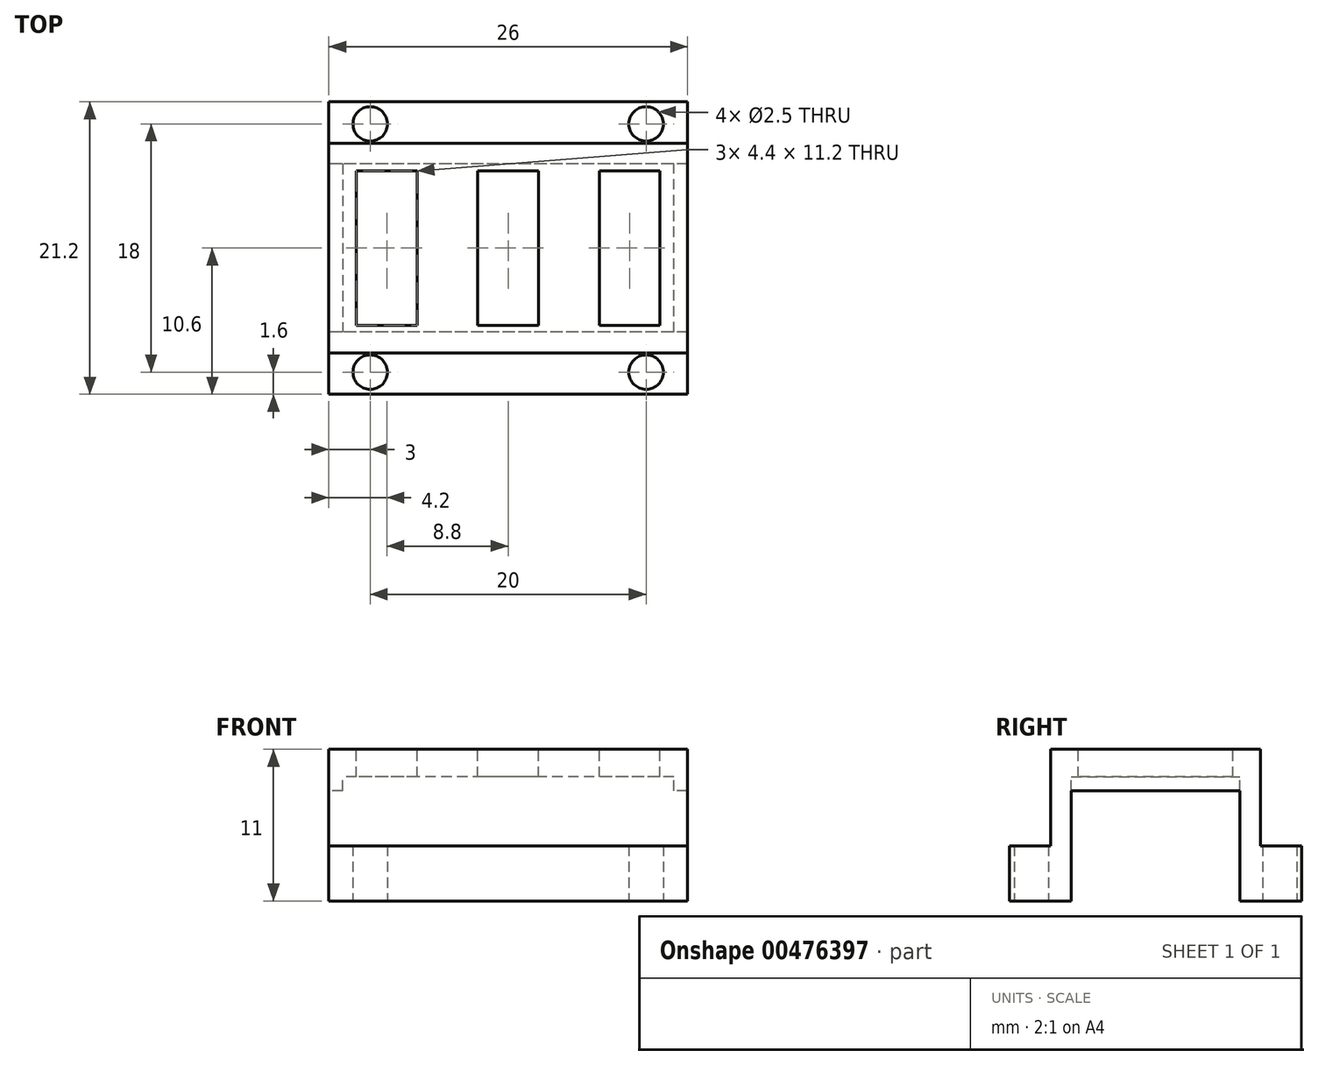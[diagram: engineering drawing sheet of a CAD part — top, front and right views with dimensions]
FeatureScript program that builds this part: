
annotation { "Feature Type Name" : "Feature", "Feature Type Description" : "" }
export const myFeature = defineFeature(function(context is Context, id is Id, definition is map)
    precondition{}
    {
        {
            var Q0;
            Q0=qCreatedBy(makeId("Right.planeOp"),FACE);
            var sketch = newSketch(context, id + "F0", { "sketchPlane" : qUnion([Q0])});
            skLineSegment(sketch, "E0", {"start": v(0, 0) * mm, "end": v(4.5, 0) * mm});
            skLineSegment(sketch, "E1", {"start": v(4.5, 0) * mm, "end": v(4.5, 9) * mm});
            skLineSegment(sketch, "E2", {"start": v(4.5, 9) * mm, "end": v(10.6, 9) * mm});
            skLineSegment(sketch, "E3", {"start": v(10.6, 9) * mm, "end": v(10.6, 11) * mm, "construction": true});
            skLineSegment(sketch, "E4", {"start": v(10.6, 11) * mm, "end": v(3, 11) * mm});
            skLineSegment(sketch, "E5", {"start": v(3, 11) * mm, "end": v(3, 4) * mm});
            skLineSegment(sketch, "E6", {"start": v(3, 4) * mm, "end": v(0, 4) * mm});
            skLineSegment(sketch, "E7", {"start": v(0, 4) * mm, "end": v(0, 0) * mm});
            skLineSegment(sketch, "E8.0.MirrorCS", {"start": v(21.2, 0) * mm, "end": v(16.7, 0) * mm});
            skLineSegment(sketch, "E8.1.MirrorCS", {"start": v(16.7, 0) * mm, "end": v(16.7, 9) * mm});
            skLineSegment(sketch, "E8.2.MirrorCS", {"start": v(16.7, 9) * mm, "end": v(10.6, 9) * mm});
            skLineSegment(sketch, "E8.3.MirrorCS", {"start": v(10.6, 11) * mm, "end": v(18.2, 11) * mm});
            skLineSegment(sketch, "E8.4.MirrorCS", {"start": v(18.2, 11) * mm, "end": v(18.2, 4) * mm});
            skLineSegment(sketch, "E8.5.MirrorCS", {"start": v(21.2, 4) * mm, "end": v(21.2, 0) * mm});
            skLineSegment(sketch, "E8.6.MirrorCS", {"start": v(18.2, 4) * mm, "end": v(21.2, 4) * mm});
            skSolve(sketch);
        }
        {
            var Q0;
            Q0=qSketchRegion(id+"F0",true);
            extrude(context, id + "F1", {"entities" : qUnion([Q0]), "depth" : 26 * mm});
        }
        {
            var Q0;
            Q0=makeQuery(id+"F1.opExtrude","SWEPT_FACE",FACE,{"disambiguationData":[OSD([sQuery(id+"F0.wireOp",EDGE,"E2"),sQuery(id+"F0.wireOp",EDGE,"E8.2.MirrorCS")])]});
            var sketch = newSketch(context, id + "F2", { "sketchPlane" : qUnion([Q0])});
            skLineSegment(sketch, "E9.bottom", {"start": v(0, -16.7) * mm, "end": v(1, -16.7) * mm});
            skLineSegment(sketch, "E9.top", {"start": v(0, -4.5) * mm, "end": v(1, -4.5) * mm});
            skLineSegment(sketch, "E9.left", {"start": v(0, -16.7) * mm, "end": v(0, -4.5) * mm});
            skLineSegment(sketch, "E9.right", {"start": v(1, -16.7) * mm, "end": v(1, -4.5) * mm});
            skLineSegment(sketch, "E10.bottom", {"start": v(26, -4.5) * mm, "end": v(25, -4.5) * mm});
            skLineSegment(sketch, "E10.top", {"start": v(26, -16.7) * mm, "end": v(25, -16.7) * mm});
            skLineSegment(sketch, "E10.left", {"start": v(26, -4.5) * mm, "end": v(26, -16.7) * mm});
            skLineSegment(sketch, "E10.right", {"start": v(25, -4.5) * mm, "end": v(25, -16.7) * mm});
            skSolve(sketch);
        }
        {
            var Q0;
            Q0=qSketchRegion(id+"F2",true);
            extrude(context, id + "F3", {"entities" : qUnion([Q0]), "operationType" : NewBodyOperationType.ADD, "depth" : 1 * mm});
        }
        {
            var Q0;
            Q0=makeQuery(id+"F1.opExtrude","SWEPT_FACE",FACE,{"disambiguationData":[OSD([sQuery(id+"F0.wireOp",EDGE,"E0")])]});
            var sketch = newSketch(context, id + "F4", { "sketchPlane" : qUnion([Q0])});
            skCircle(sketch, "E11", {"center": v(3, -1.6) * mm, "radius": 1.25 * mm});
            skLineSegment(sketch, "E12", {"start": v(13, 0) * mm, "end": v(13, -10.6) * mm, "construction": true});
            skLineSegment(sketch, "E13", {"start": v(13, -10.6) * mm, "end": v(0, -10.6) * mm, "construction": true});
            skLineSegment(sketch, "E14", {"start": v(0, -10.6) * mm, "end": v(0, 0) * mm, "construction": true});
            skLineSegment(sketch, "E15", {"start": v(0, -10.6) * mm, "end": v(0, -21.2) * mm, "construction": true});
            skCircle(sketch, "E16.0.MirrorC", {"center": v(23, -1.6) * mm, "radius": 1.25 * mm});
            skCircle(sketch, "E17.0.MirrorC", {"center": v(23, -19.6) * mm, "radius": 1.25 * mm});
            skCircle(sketch, "E17.1.MirrorC", {"center": v(3, -19.6) * mm, "radius": 1.25 * mm});
            skSolve(sketch);
        }
        {
            var Q0;
            Q0=qSketchRegion(id+"F4",true);
            extrude(context, id + "F5", {"entities" : qUnion([Q0]), "operationType" : NewBodyOperationType.REMOVE, "endBound" : BoundingType.UP_TO_NEXT, "oppositeDirection" : true, "depth" : 25 * mm});
        }
        {
            var Q0;
            Q0=makeQuery(id+"F1.opExtrude","SWEPT_FACE",FACE,{"disambiguationData":[OSD([sQuery(id+"F0.wireOp",EDGE,"E4"),sQuery(id+"F0.wireOp",EDGE,"E8.3.MirrorCS")])]});
            var sketch = newSketch(context, id + "F6", { "sketchPlane" : qUnion([Q0])});
            skLineSegment(sketch, "E18.bottom", {"start": v(6.4, 5) * mm, "end": v(10.8, 5) * mm, "construction": true});
            skLineSegment(sketch, "E18.left", {"start": v(2, 5) * mm, "end": v(2, 16.2) * mm});
            skLineSegment(sketch, "E18.right", {"start": v(10.8, 5) * mm, "end": v(10.8, 16.2) * mm});
            skLineSegment(sketch, "E19.top", {"start": v(10.8, 5) * mm, "end": v(15.2, 5) * mm});
            skLineSegment(sketch, "E19.left", {"start": v(10.8, 16.2) * mm, "end": v(10.8, 5) * mm});
            skLineSegment(sketch, "E20.bottom", {"start": v(15.2, 5) * mm, "end": v(19.6, 5) * mm, "construction": true});
            skLineSegment(sketch, "E20.left", {"start": v(15.2, 5) * mm, "end": v(15.2, 16.2) * mm});
            skLineSegment(sketch, "E20.right", {"start": v(19.6, 5) * mm, "end": v(19.6, 16.2) * mm});
            skLineSegment(sketch, "E21.bottom", {"start": v(19.6, 16.2) * mm, "end": v(24, 16.2) * mm});
            skLineSegment(sketch, "E21.top", {"start": v(19.6, 5) * mm, "end": v(24, 5) * mm});
            skLineSegment(sketch, "E21.left", {"start": v(19.6, 16.2) * mm, "end": v(19.6, 5) * mm});
            skLineSegment(sketch, "E21.right", {"start": v(24, 16.2) * mm, "end": v(24, 5) * mm});
            skLineSegment(sketch, "E22", {"start": v(2, 16.2) * mm, "end": v(0, 16.2) * mm, "construction": true});
            skLineSegment(sketch, "E23", {"start": v(24, 16.2) * mm, "end": v(26, 16.2) * mm, "construction": true});
            skLineSegment(sketch, "E24", {"start": v(13, 16.2) * mm, "end": v(13, 18.2) * mm, "construction": true});
            skLineSegment(sketch, "E25", {"start": v(13, 5) * mm, "end": v(13, 3) * mm, "construction": true});
            skLineSegment(sketch, "E26", {"start": v(6.4, 5) * mm, "end": v(6.4, 16.2) * mm});
            skLineSegment(sketch, "E27", {"start": v(2, 16.2) * mm, "end": v(6.4, 16.2) * mm});
            skLineSegment(sketch, "E28", {"start": v(6.4, 16.2) * mm, "end": v(10.8, 16.2) * mm, "construction": true});
            skLineSegment(sketch, "E29", {"start": v(10.8, 16.2) * mm, "end": v(15.2, 16.2) * mm});
            skLineSegment(sketch, "E30", {"start": v(19.6, 16.2) * mm, "end": v(15.2, 16.2) * mm, "construction": true});
            skLineSegment(sketch, "E31", {"start": v(2, 5) * mm, "end": v(6.4, 5) * mm});
            skSolve(sketch);
        }
        {
            var Q0;
            Q0=qSketchRegion(id+"F6",true);
            extrude(context, id + "F7", {"entities" : qUnion([Q0]), "operationType" : NewBodyOperationType.REMOVE, "endBound" : BoundingType.UP_TO_NEXT, "oppositeDirection" : true, "depth" : 25 * mm});
        }
    });
